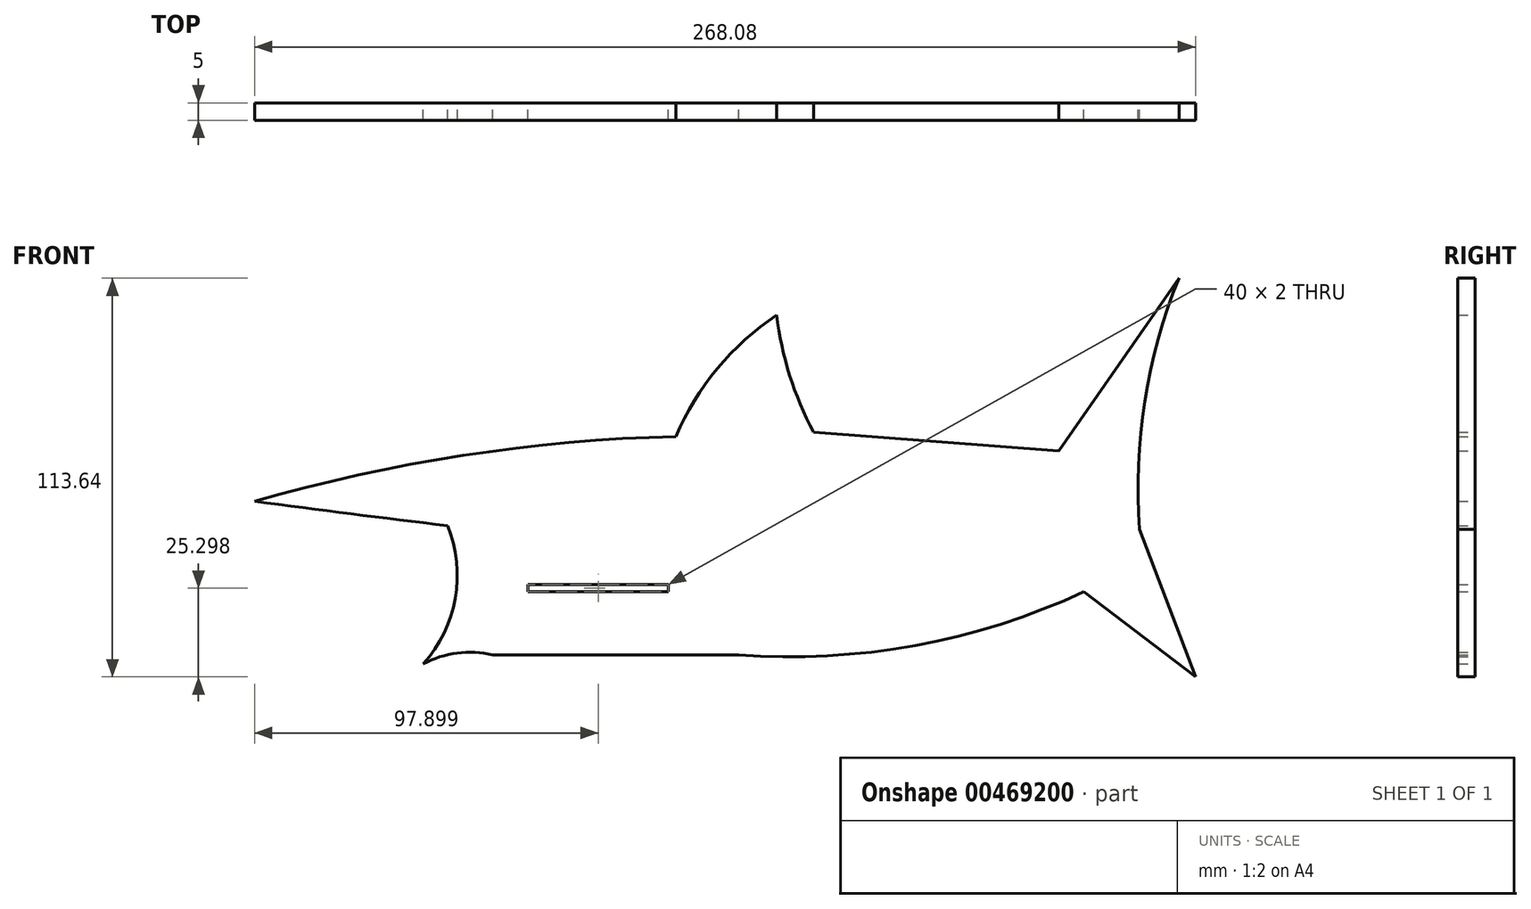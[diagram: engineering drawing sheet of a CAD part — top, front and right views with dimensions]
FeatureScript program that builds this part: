
annotation { "Feature Type Name" : "Feature", "Feature Type Description" : "" }
export const myFeature = defineFeature(function(context is Context, id is Id, definition is map)
    precondition{}
    {
        {
            var Q0;
            Q0=qCreatedBy(makeId("Front.planeOp"),FACE);
            var sketch = newSketch(context, id + "F0", { "sketchPlane" : qUnion([Q0])});
            skLineSegment(sketch, "E0", {"start": v(-5.68, 33.34) * mm, "end": v(64.11, 28) * mm});
            skPoint(sketch, "E1", {"position": v(-5.68, 33.34) * mm});
            skPoint(sketch, "E2", {"position": v(-16.2, 66.72) * mm});
            skArc(sketch, "E3", {"start": v(-16.2, 66.72) * mm, "mid": v(-12.52, 49.53) * mm, "end": v(-5.68, 33.34) * mm});
            skPoint(sketch, "E4", {"position": v(-44.98, 32.13) * mm});
            skArc(sketch, "E5", {"start": v(-16.2, 66.72) * mm, "mid": v(-33.1, 51.53) * mm, "end": v(-44.98, 32.13) * mm});
            skPoint(sketch, "E6", {"position": v(-164.98, 13.62) * mm});
            skArc(sketch, "E7", {"start": v(-44.98, 32.13) * mm, "mid": v(-105.57, 26.71) * mm, "end": v(-164.98, 13.62) * mm});
            skPoint(sketch, "E8", {"position": v(-109.98, 6.69) * mm});
            skArc(sketch, "E9", {"start": v(-164.98, 13.62) * mm, "mid": v(-137.5, 10.07) * mm, "end": v(-109.98, 6.69) * mm});
            skPoint(sketch, "E10", {"position": v(-116.9, -32.7) * mm});
            skArc(sketch, "E11", {"start": v(-116.9, -32.7) * mm, "mid": v(-107.78, -14) * mm, "end": v(-109.98, 6.69) * mm});
            skPoint(sketch, "E12", {"position": v(-97.07, -30.1) * mm});
            skArc(sketch, "E13", {"start": v(-97.07, -30.1) * mm, "mid": v(-107.22, -29.62) * mm, "end": v(-116.9, -32.7) * mm});
            skLineSegment(sketch, "E14", {"start": v(-97.07, -30.1) * mm, "end": v(-27.07, -30.1) * mm});
            skPoint(sketch, "E15", {"position": v(71.3, -12.14) * mm});
            skArc(sketch, "E16", {"start": v(-27.07, -30.1) * mm, "mid": v(23.27, -27.47) * mm, "end": v(71.3, -12.14) * mm});
            skLineSegment(sketch, "E17", {"start": v(71.3, -12.14) * mm, "end": v(103.1, -36.4) * mm});
            skLineSegment(sketch, "E18", {"start": v(103.1, -36.4) * mm, "end": v(87.2, 5.7) * mm});
            skPoint(sketch, "E18.endSnap0", {"position": v(87.2, -24.27) * mm});
            skLineSegment(sketch, "E19", {"start": v(64.11, 28) * mm, "end": v(98.4, 77.24) * mm});
            skArc(sketch, "E20", {"start": v(98.4, 77.24) * mm, "mid": v(88.7, 42.1) * mm, "end": v(87.2, 5.7) * mm});
            skPoint(sketch, "E21", {"position": v(-87.08, -10.1) * mm});
            skPoint(sketch, "E22", {"position": v(-47.08, -10.1) * mm});
            skPoint(sketch, "E23", {"position": v(-87.08, -12.1) * mm});
            skPoint(sketch, "E24", {"position": v(-47.08, -12.1) * mm});
            skLineSegment(sketch, "E25", {"start": v(-47.08, -10.1) * mm, "end": v(-47.08, -12.1) * mm});
            skLineSegment(sketch, "E26", {"start": v(-87.08, -12.1) * mm, "end": v(-87.08, -10.1) * mm});
            skLineSegment(sketch, "E27", {"start": v(-87.08, -12.1) * mm, "end": v(-47.08, -12.1) * mm});
            skLineSegment(sketch, "E28", {"start": v(-87.08, -10.1) * mm, "end": v(-47.08, -10.1) * mm});
            skSolve(sketch);
        }
        {
            var Q0;
            Q0=makeQuery(id+"F0.imprint","IMPRINT",FACE,{"disambiguationData":[TD([[makeQuery(id+"F0.imprint","IMPRINT",EDGE,{"derivedFrom":sQuery(id+"F0.wireOp",EDGE,"E0")}),-1.0]])]});
            extrude(context, id + "F1", {"entities" : qUnion([Q0]), "depth" : 5 * mm});
        }
    });
